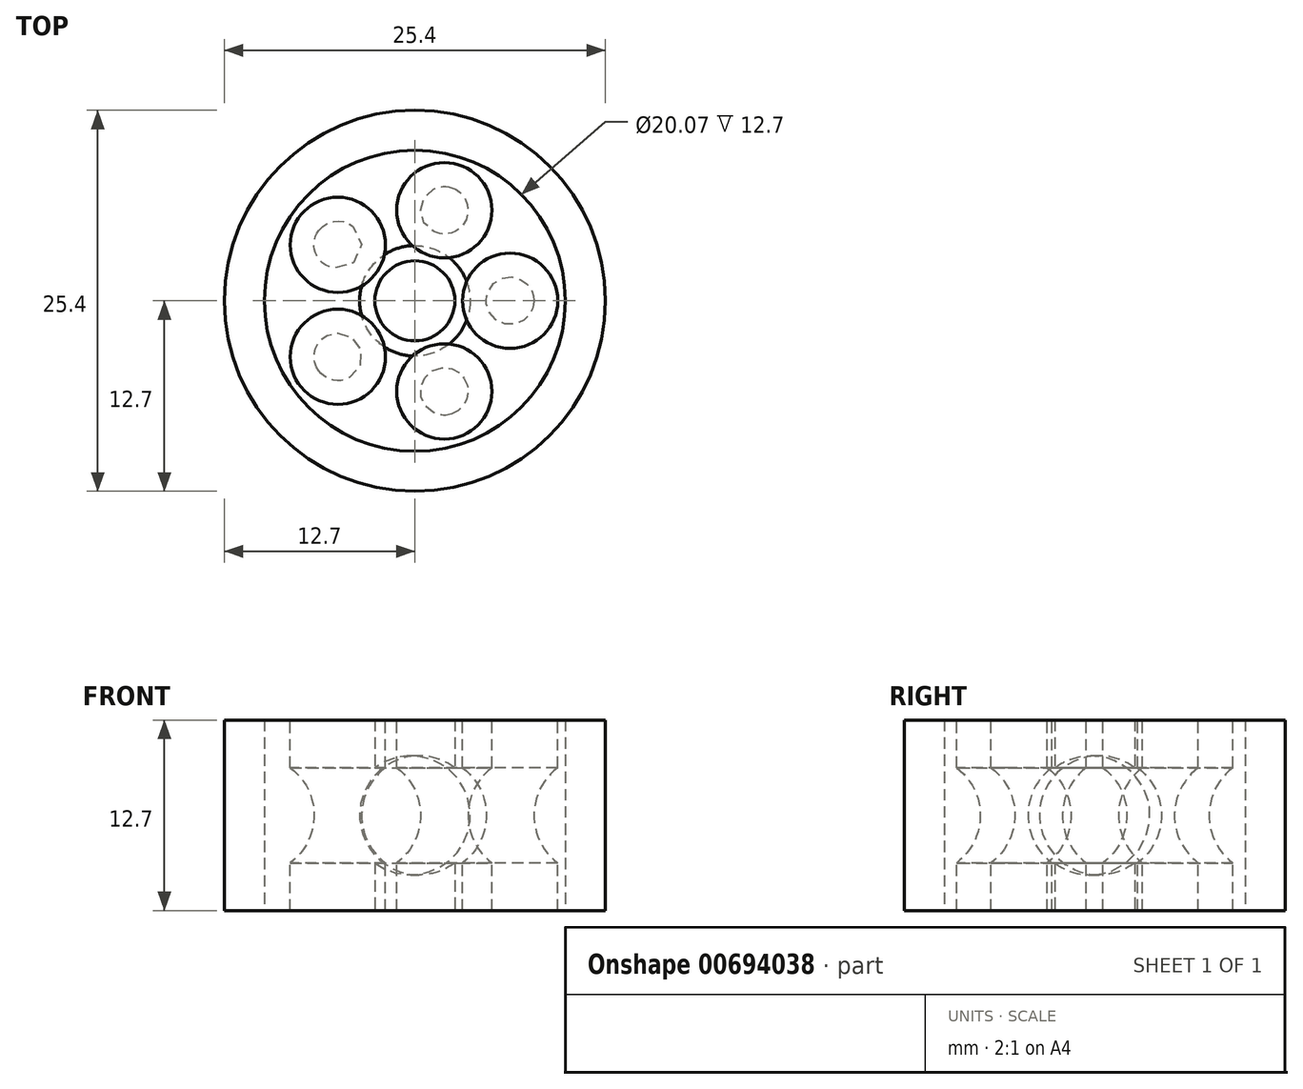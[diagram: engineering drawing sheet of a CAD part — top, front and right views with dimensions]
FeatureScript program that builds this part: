
annotation { "Feature Type Name" : "Feature", "Feature Type Description" : "" }
export const myFeature = defineFeature(function(context is Context, id is Id, definition is map)
    precondition{}
    {
        {
            var Q0;
            Q0=qCreatedBy(makeId("Front.planeOp"),FACE);
            var sketch = newSketch(context, id + "F0", { "sketchPlane" : qUnion([Q0])});
            skLineSegment(sketch, "E0.bottom", {"start": v(0, 0) * mm, "end": v(2.67, 0) * mm});
            skLineSegment(sketch, "E0.top", {"start": v(0, 12.7) * mm, "end": v(2.67, 12.7) * mm});
            skLineSegment(sketch, "E0.left", {"start": v(0, 0) * mm, "end": v(0, 12.7) * mm});
            skLineSegment(sketch, "E1", {"start": v(3.18, 0) * mm, "end": v(6.35, 0) * mm});
            skLineSegment(sketch, "E2", {"start": v(9.53, 0) * mm, "end": v(12.7, 0) * mm});
            skLineSegment(sketch, "E3", {"start": v(12.7, 0) * mm, "end": v(12.7, 12.7) * mm});
            skLineSegment(sketch, "E4", {"start": v(12.7, 12.7) * mm, "end": v(10.03, 12.7) * mm});
            skLineSegment(sketch, "E5", {"start": v(2.67, 12.7) * mm, "end": v(2.67, 9.53) * mm});
            skLineSegment(sketch, "E6", {"start": v(3.18, 0) * mm, "end": v(3.18, 3.18) * mm});
            skLineSegment(sketch, "E7", {"start": v(10.03, 0) * mm, "end": v(10.03, 12.7) * mm});
            skArc(sketch, "E8", {"start": v(3.18, 3.17) * mm, "mid": v(4.76, 6.35) * mm, "end": v(3.18, 9.53) * mm});
            skPoint(sketch, "E9.endSnap0", {"position": v(2.67, 6.35) * mm});
            skLineSegment(sketch, "E10.trimOffspring", {"start": v(3.18, 9.53) * mm, "end": v(3.18, 12.7) * mm});
            skArc(sketch, "E11", {"start": v(2.67, 3.17) * mm, "mid": v(4.25, 6.35) * mm, "end": v(2.67, 9.53) * mm});
            skPoint(sketch, "E9.end.orphan", {"position": v(4.25, 6.35) * mm});
            skPoint(sketch, "E9.start.orphan", {"position": v(2.67, 6.35) * mm});
            skLineSegment(sketch, "E12.trimOffspring", {"start": v(2.67, 3.17) * mm, "end": v(2.67, 0) * mm});
            skLineSegment(sketch, "E13", {"start": v(3.18, 12.7) * mm, "end": v(6.35, 12.7) * mm});
            skLineSegment(sketch, "E14", {"start": v(6.35, 12.7) * mm, "end": v(6.35, 0) * mm});
            skPoint(sketch, "E15.start.orphan", {"position": v(9.53, 12.7) * mm});
            skSolve(sketch);
        }
        {
            var Q0;
            Q0=makeQuery(id+"F0.imprint","IMPRINT",FACE,{"disambiguationData":[TD([[makeQuery(id+"F0.imprint","IMPRINT",EDGE,{"derivedFrom":sQuery(id+"F0.wireOp",EDGE,"E1")}),1.0]])]});
            var Q1;
            Q1=sQuery(id+"F0.wireOp",EDGE,"E14");
            revolve(context, id + "F1", {"surfaceOperationType" : NewSurfaceOperationType.NEW, "entities" : qUnion([Q0]), "axis" : qUnion([Q1]), "revolveType" : RevolveType.FULL});
        }
        {
            var Q0;
            Q0=makeQuery(id+"F0.imprint","IMPRINT",FACE,{"disambiguationData":[TD([[makeQuery(id+"F0.imprint","IMPRINT",EDGE,{"derivedFrom":sQuery(id+"F0.wireOp",EDGE,"E0.bottom")}),1.0]])]});
            var Q1;
            {var subQ0=sQuery(id+"F0.wireOp",EDGE,"E3");Q1=makeQuery(id+"F0.imprint","IMPRINT",FACE,{"disambiguationData":[TD([[makeQuery(id+"F0.imprint","IMPRINT",EDGE,{"derivedFrom":subQ0}),1.0]])]});}
            var Q2;
            Q2=sQuery(id+"F0.wireOp",EDGE,"E0.left");
            revolve(context, id + "F2", {"surfaceOperationType" : NewSurfaceOperationType.NEW, "entities" : qUnion([Q0, Q1]), "axis" : qUnion([Q2]), "revolveType" : RevolveType.FULL});
        }
        {
            var Q0;
            Q0=makeQuery(id+"F1.opRevolve","SWEPT_BODY",BODY,{"disambiguationData":[OSD([sQuery(id+"F0.wireOp",EDGE,"E1"),sQuery(id+"F0.wireOp",EDGE,"E6"),sQuery(id+"F0.wireOp",EDGE,"E8"),sQuery(id+"F0.wireOp",EDGE,"E10.trimOffspring"),sQuery(id+"F0.wireOp",EDGE,"E13"),sQuery(id+"F0.wireOp",EDGE,"E14")])]});
            var Q1;
            Q1=sQuery(id+"F0.wireOp",EDGE,"E0.left");
            circularPattern(context, id + "F3", {"entities" : qUnion([Q0]), "axis" : qUnion([Q1]), "angle" : 360 * degree, "instanceCount" : 5, "equalSpace" : true});
        }
    });
